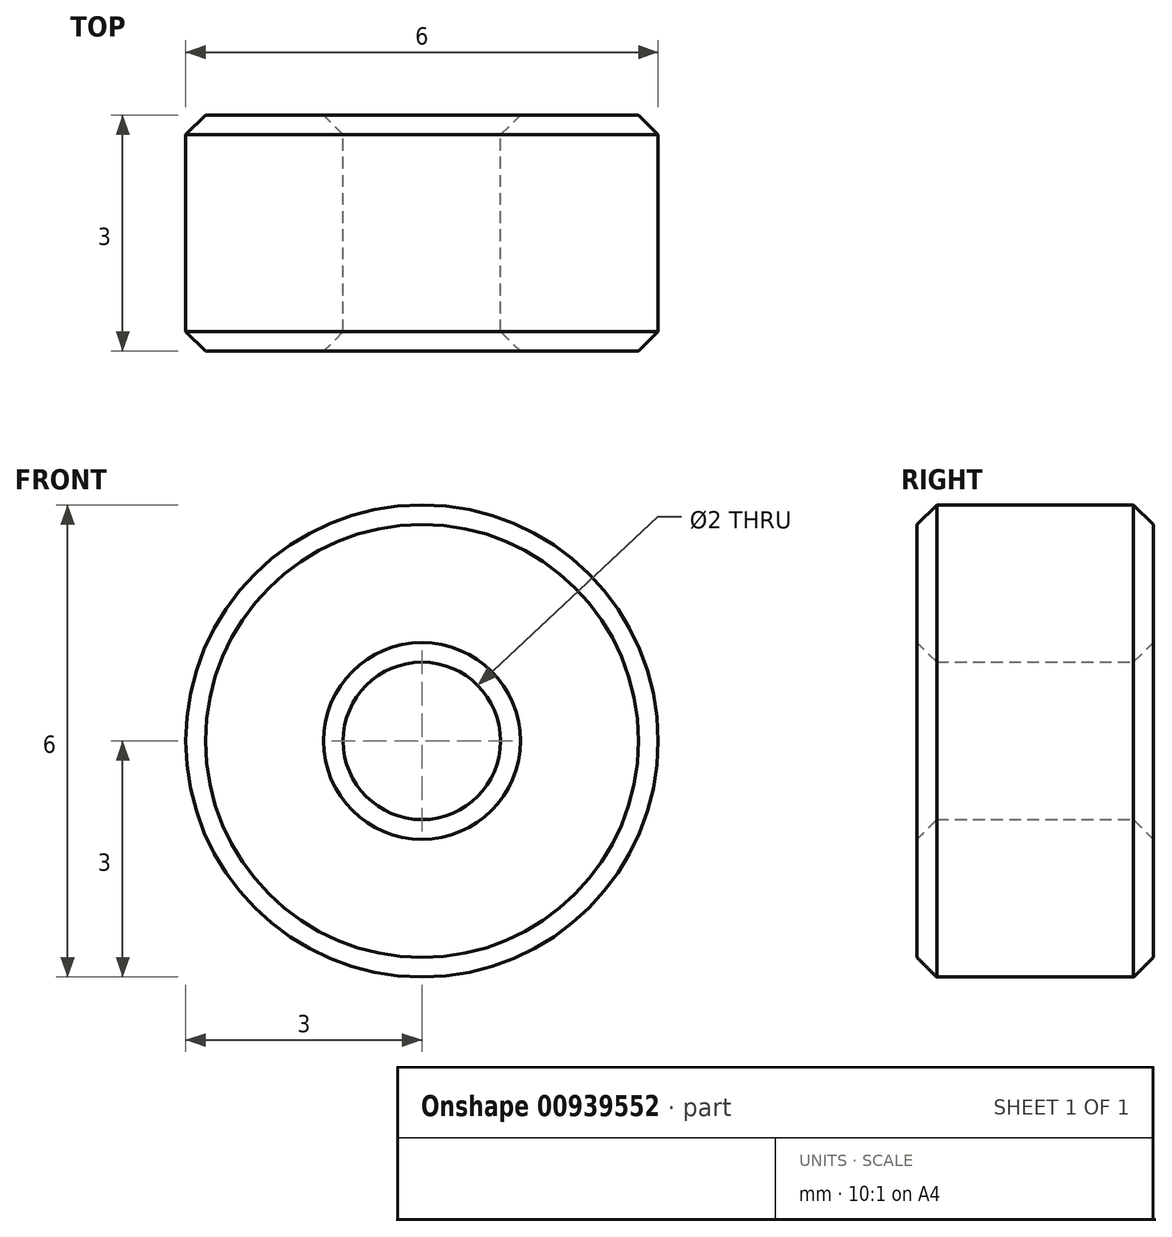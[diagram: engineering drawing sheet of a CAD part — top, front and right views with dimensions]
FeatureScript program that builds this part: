
annotation { "Feature Type Name" : "Feature", "Feature Type Description" : "" }
export const myFeature = defineFeature(function(context is Context, id is Id, definition is map)
    precondition{}
    {
        {
            var Q0;
            Q0=qCreatedBy(makeId("Front.planeOp"),FACE);
            var sketch = newSketch(context, id + "F0", { "sketchPlane" : qUnion([Q0])});
            skCircle(sketch, "E0", {"center": v(0, 0) * mm, "radius": 1 * mm});
            skCircle(sketch, "E1", {"center": v(0, 0) * mm, "radius": 3 * mm});
            skSolve(sketch);
        }
        {
            var Q0;
            Q0=makeQuery(id+"F0.imprint","IMPRINT",FACE,{"disambiguationData":[TD([[makeQuery(id+"F0.imprint","IMPRINT",EDGE,{"derivedFrom":sQuery(id+"F0.wireOp",EDGE,"E0")}),-1.0]])]});
            extrude(context, id + "F1", {"entities" : qUnion([Q0]), "depth" : 3 * mm, "offsetDistance" : 25 * mm});
        }
        {
            var Q0;
            Q0=makeQuery(id+"F1.opExtrude","CAP_EDGE",EDGE,{"disambiguationData":[OSD([sQuery(id+"F0.wireOp",EDGE,"E1")])],"isStart":false});
            var Q1;
            Q1=makeQuery(id+"F1.opExtrude","CAP_EDGE",EDGE,{"disambiguationData":[OSD([sQuery(id+"F0.wireOp",EDGE,"E1")])],"isStart":true});
            var Q2;
            Q2=makeQuery(id+"F1.opExtrude","CAP_EDGE",EDGE,{"disambiguationData":[OSD([sQuery(id+"F0.wireOp",EDGE,"E0")])],"isStart":false});
            var Q3;
            Q3=makeQuery(id+"F1.opExtrude","CAP_EDGE",EDGE,{"disambiguationData":[OSD([sQuery(id+"F0.wireOp",EDGE,"E0")])],"isStart":true});
            chamfer(context, id + "F2", {"entities" : qUnion([Q0, Q1, Q2, Q3]), "width" : .25 * mm, "tangentPropagation" : true});
        }
    });
